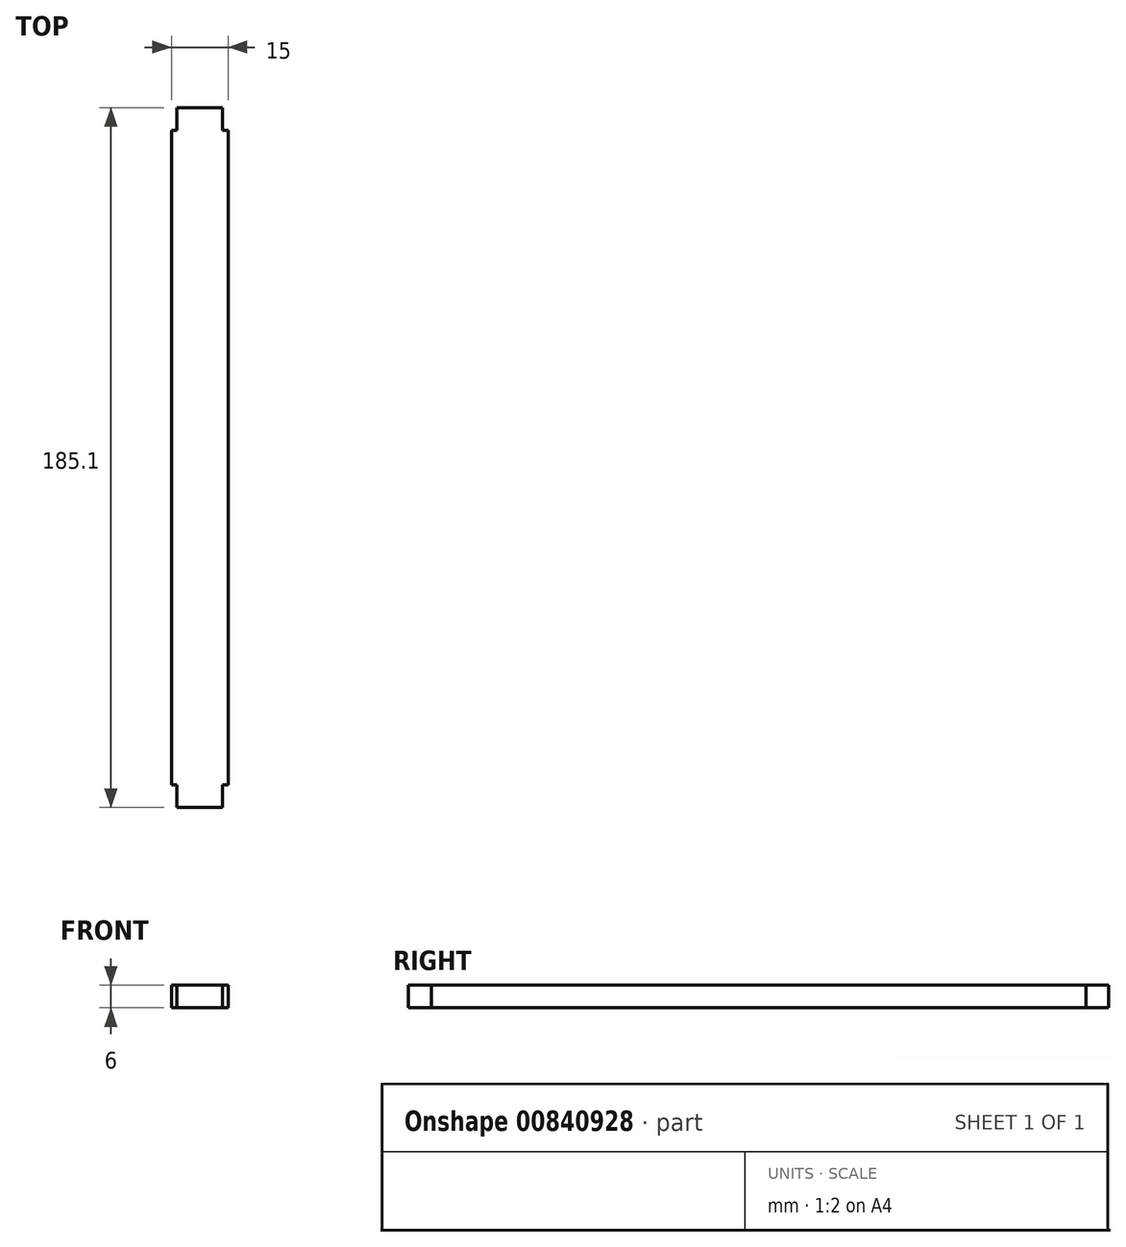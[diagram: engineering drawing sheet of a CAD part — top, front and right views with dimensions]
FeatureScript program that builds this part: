
annotation { "Feature Type Name" : "Feature", "Feature Type Description" : "" }
export const myFeature = defineFeature(function(context is Context, id is Id, definition is map)
    precondition{}
    {
        {
            var Q0;
            Q0=qCreatedBy(makeId("Top.planeOp"),FACE);
            var sketch = newSketch(context, id + "F0", { "sketchPlane" : qUnion([Q0])});
            skLineSegment(sketch, "E0", {"start": v(-17.4, 0) * mm, "end": v(22.4, 0) * mm, "construction": true});
            skLineSegment(sketch, "E1", {"start": v(-7.5, 0) * mm, "end": v(-7.5, 86.55) * mm});
            skLineSegment(sketch, "E2", {"start": v(-7.5, 86.55) * mm, "end": v(-6, 86.55) * mm});
            skLineSegment(sketch, "E3", {"start": v(-6, 86.55) * mm, "end": v(-6, 92.55) * mm});
            skLineSegment(sketch, "E4", {"start": v(-6, 92.55) * mm, "end": v(0, 92.55) * mm});
            skLineSegment(sketch, "E5", {"start": v(0, 92.55) * mm, "end": v(0, 0) * mm, "construction": true});
            skLineSegment(sketch, "E6.MirrorCS", {"start": v(7.5, 86.55) * mm, "end": v(6, 86.55) * mm});
            skLineSegment(sketch, "E7.MirrorCS", {"start": v(6, 86.55) * mm, "end": v(6, 92.55) * mm});
            skLineSegment(sketch, "E8.MirrorCS", {"start": v(6, 92.55) * mm, "end": v(0, 92.55) * mm});
            skLineSegment(sketch, "E9.MirrorCS", {"start": v(7.5, 0) * mm, "end": v(7.5, 86.55) * mm});
            skLineSegment(sketch, "E10.MirrorCS", {"start": v(-7.5, -86.55) * mm, "end": v(-6, -86.55) * mm});
            skLineSegment(sketch, "E11.MirrorCS", {"start": v(6, -86.55) * mm, "end": v(6, -92.55) * mm});
            skLineSegment(sketch, "E12.MirrorCS", {"start": v(-6, -86.55) * mm, "end": v(-6, -92.55) * mm});
            skLineSegment(sketch, "E13.MirrorCS", {"start": v(7.5, -86.55) * mm, "end": v(6, -86.55) * mm});
            skLineSegment(sketch, "E14.MirrorCS", {"start": v(-6, -92.55) * mm, "end": v(0, -92.55) * mm});
            skLineSegment(sketch, "E15.MirrorCS", {"start": v(6, -92.55) * mm, "end": v(0, -92.55) * mm});
            skLineSegment(sketch, "E16.MirrorCS", {"start": v(-7.5, 0) * mm, "end": v(-7.5, -86.55) * mm});
            skLineSegment(sketch, "E17.MirrorCS", {"start": v(0, -92.55) * mm, "end": v(0, 0) * mm, "construction": true});
            skLineSegment(sketch, "E18.MirrorCS", {"start": v(7.5, 0) * mm, "end": v(7.5, -86.55) * mm});
            skSolve(sketch);
        }
        {
            var Q0;
            Q0=qSketchRegion(id+"F0",true);
            extrude(context, id + "F1", {"entities" : qUnion([Q0]), "depth" : 6 * mm, "offsetDistance" : 25 * mm});
        }
    });
